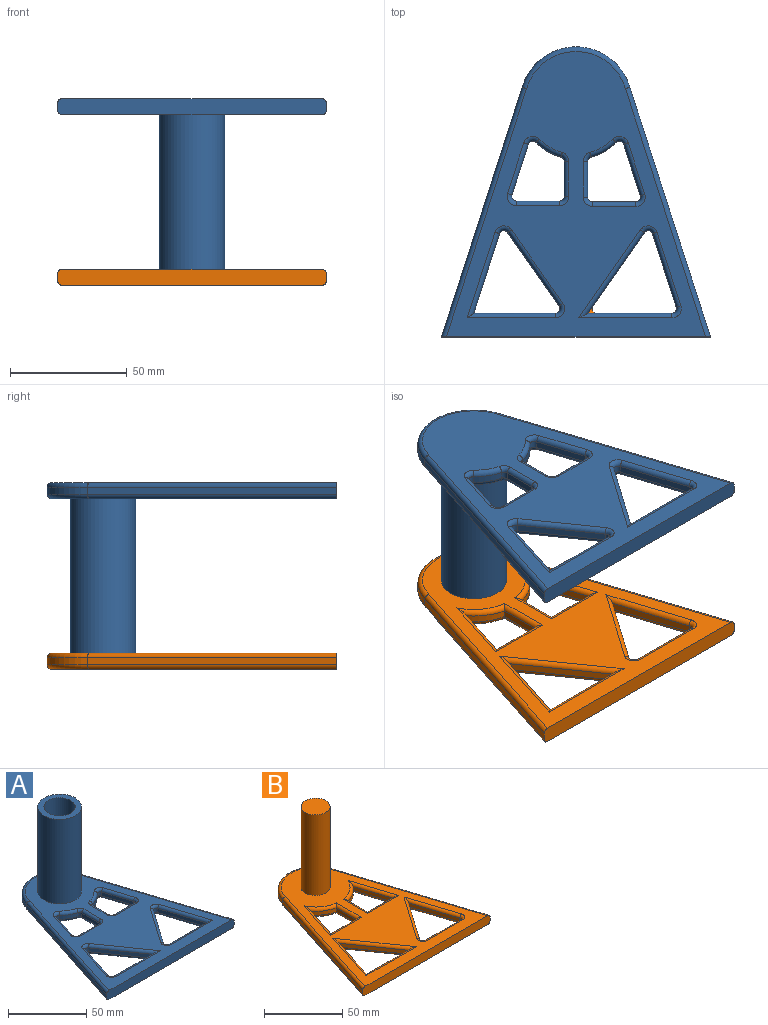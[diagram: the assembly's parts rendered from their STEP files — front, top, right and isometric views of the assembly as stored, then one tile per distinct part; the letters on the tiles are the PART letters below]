
ASSEMBLY  parts=2 mates=1
PART A: 100 faces, bbox 115x126.6x73 mm
  f0: cylinder r=24mm len=10.61mm, axis (0,0,-1), area 37.4mm2, adj f68,f73,f76,f79
  f1: plane 21.71x7.01mm, normal (-0.95,-0.31,0), area 68.4mm2, adj f66,f67,f75,f76
  f2: plane 18.51x3mm, normal (0,1,0), area 55.5mm2, adj f60,f64,f65,f66
  f3: plane 34.05x10.99mm, normal (-0.95,-0.31,0), area 107.3mm2, adj f4,f48,f53,f58
  f4: plane 34.92x3mm, normal (0,1,0), area 104.8mm2, adj f3,f50,f55,f59
  f5: plane 22.05x7.12mm, normal (0.95,-0.31,0), area 69.5mm2, adj f83,f84,f93,f94
  f6: cylinder r=24mm len=10.61mm, axis (0,0,-1), area 37.4mm2, adj f88,f93,f96,f99
  f7: plane 15.28x3mm, normal (-1,0,0), area 45.8mm2, adj f86,f87,f95,f96
  f8: plane 115x7mm, normal (0,-1,0), area 801.4mm2, adj f9,f15,f18,f19,f36,f38,f41,f47
  f9: plane 106.63x34.43mm, normal (0.95,0.31,0), area 336.1mm2, adj f8,f36,f40,f41
  f10: cylinder r=24mm len=46.1mm, axis (0,0,-1), area 185.6mm2, adj f39,f40,f44,f45
  f11: plane 36.01x3mm, normal (0,1,0), area 108mm2, adj f16,f27,f32,f35
  f12: plane 31.43x10.15mm, normal (0.95,-0.31,0), area 99.1mm2, adj f26,f28,f31,f32
  f13: plane 31.43x22.02mm, normal (0.82,-0.57,0), area 115.1mm2, adj f49,f53,f54,f55
  f14: plane 18.62x3mm, normal (0,1,0), area 55.9mm2, adj f80,f84,f85,f86
  f15: plane 106.63x34.43mm, normal (-0.95,0.31,0), area 336.1mm2, adj f8,f38,f44,f47
  f16: plane 34.58x24.23mm, normal (-0.82,-0.57,0), area 126.7mm2, adj f11,f24,f28,f33
  f17: plane 14.94x3mm, normal (1,0,0), area 44.8mm2, adj f63,f64,f73,f74
  f18: plane 122x110.8mm, normal (0,0,1), area 4813.2mm2, adj f8,f20,f30,f31,f33,f34,f35,f41
  f19: plane 122x110.8mm, normal (0,0,-1), area 5429mm2, adj f8,f24,f25,f26,f27,f29,f36,f37
  f20: cylinder r=14mm len=66mm, axis (0,0,-1), area 5805.7mm2, adj f18,f22
  f21: cylinder r=10mm len=66mm, axis (0,0,-1), area 4146.9mm2, adj f22,f23
  f22: plane 28x28mm, normal (0,0,1), area 301.6mm2, adj f20,f21
  f23: plane 20x20mm, normal (0,0,1), area 314.2mm2, adj f21
  f24: cylinder r=2mm len=38.87mm, axis (0.57,-0.82,0), area 137mm2, adj f16,f19,f25,f27
  f25: torus R=4mm, axis (0,0,1), area 19mm2, adj f19,f24,f26,f28
  f26: cylinder r=2mm len=32.05mm, axis (0.31,0.95,0), area 103.8mm2, adj f12,f19,f25,f29
  f27: cylinder r=2mm len=39.86mm, axis (-1,0,0), area 117.5mm2, adj f11,f19,f24,f29
  f28: cylinder r=2mm len=3.54mm, axis (0,0,-1), area 13.3mm2, adj f12,f16,f25,f30
  f29: torus R=4mm, axis (0,0,1), area 16.1mm2, adj f19,f26,f27,f32
  f30: torus R=4mm, axis (0,0,1), area 19mm2, adj f18,f28,f31,f33
  f31: cylinder r=2mm len=32.05mm, axis (-0.31,-0.95,0), area 103.8mm2, adj f12,f18,f30,f34
  f32: cylinder r=2mm len=3mm, axis (0,0,1), area 11.3mm2, adj f11,f12,f29,f34
  f33: cylinder r=2mm len=38.87mm, axis (-0.57,0.82,0), area 137mm2, adj f16,f18,f30,f35
  f34: torus R=4mm, axis (0,0,1), area 16.1mm2, adj f18,f31,f32,f35
  f35: cylinder r=2mm len=39.86mm, axis (1,0,0), area 117.5mm2, adj f11,f18,f33,f34
  f36: cylinder r=2mm len=107.24mm, axis (-0.31,0.95,0), area 351.3mm2, adj f8,f9,f19,f37
  f37: torus R=4mm, axis (0,0,1), area 0.3mm2, adj f19,f36,f39,f40
  f38: cylinder r=2mm len=107.24mm, axis (-0.31,-0.95,0), area 351.3mm2, adj f8,f15,f19,f42
  f39: torus R=22mm, axis (0,0,1), area 188.4mm2, adj f10,f19,f37,f42
  f40: cylinder r=2mm len=3mm, axis (0,0,-1), area 0.2mm2, adj f9,f10,f37,f43
  f41: cylinder r=2mm len=107.24mm, axis (0.31,-0.95,0), area 351.3mm2, adj f8,f9,f18,f43
  f42: torus R=4mm, axis (0,0,1), area 0.3mm2, adj f19,f38,f39,f44
  f43: torus R=4mm, axis (0,0,1), area 0.3mm2, adj f18,f40,f41,f45
  f44: cylinder r=2mm len=3mm, axis (0,0,-1), area 0.2mm2, adj f10,f15,f42,f46
  f45: torus R=22mm, axis (0,0,1), area 188.4mm2, adj f10,f18,f43,f46
  f46: torus R=4mm, axis (0,0,1), area 0.3mm2, adj f18,f44,f45,f47
  f47: cylinder r=2mm len=107.24mm, axis (0.31,0.95,0), area 351.3mm2, adj f8,f15,f18,f46
  f48: cylinder r=2mm len=37.27mm, axis (0.31,-0.95,0), area 115.5mm2, adj f3,f19,f50,f51
  f49: cylinder r=2mm len=32.58mm, axis (0.57,0.82,0), area 120.6mm2, adj f13,f19,f51,f52
  f50: cylinder r=2mm len=37.67mm, axis (-1,0,0), area 112.8mm2, adj f4,f19,f48,f52
  f51: torus R=4mm, axis (0,0,1), area 19mm2, adj f19,f48,f49,f53
  f52: torus R=4mm, axis (0,0,1), area 18.7mm2, adj f19,f49,f50,f55
  f53: cylinder r=2mm len=3.54mm, axis (0,0,-1), area 13.3mm2, adj f3,f13,f51,f56
  f54: cylinder r=2mm len=32.58mm, axis (-0.57,-0.82,0), area 120.6mm2, adj f13,f18,f56,f57
  f55: cylinder r=2mm len=3.15mm, axis (0,0,-1), area 13.1mm2, adj f4,f13,f52,f57
  f56: torus R=4mm, axis (0,0,1), area 19mm2, adj f18,f53,f54,f58
  f57: torus R=4mm, axis (0,0,1), area 18.7mm2, adj f18,f54,f55,f59
  f58: cylinder r=2mm len=37.27mm, axis (-0.31,0.95,0), area 115.5mm2, adj f3,f18,f56,f59
  f59: cylinder r=2mm len=37.67mm, axis (1,0,0), area 112.8mm2, adj f4,f18,f57,f58
  f60: cylinder r=2mm len=18.51mm, axis (-1,0,0), area 58.1mm2, adj f2,f19,f61,f62
  f61: torus R=4mm, axis (0,0,1), area 13.5mm2, adj f19,f60,f63,f64
  f62: torus R=4mm, axis (0,0,1), area 16.1mm2, adj f19,f60,f66,f67
  f63: cylinder r=2mm len=14.94mm, axis (0,1,0), area 46.9mm2, adj f17,f19,f61,f69
  f64: cylinder r=2mm len=3mm, axis (0,0,-1), area 9.4mm2, adj f2,f17,f61,f70
  f65: cylinder r=2mm len=18.51mm, axis (1,0,0), area 58.1mm2, adj f2,f18,f70,f71
  f66: cylinder r=2mm len=3mm, axis (0,0,1), area 11.3mm2, adj f1,f2,f62,f71
  f67: cylinder r=2mm len=22.32mm, axis (0.31,-0.95,0), area 71.7mm2, adj f1,f19,f62,f72
  f68: torus R=22mm, axis (0,0,1), area 37.9mm2, adj f0,f19,f69,f72
  f69: torus R=4mm, axis (0,0,1), area 11.1mm2, adj f19,f63,f68,f73
  f70: torus R=4mm, axis (0,0,1), area 13.5mm2, adj f18,f64,f65,f74
  f71: torus R=4mm, axis (0,0,1), area 16.1mm2, adj f18,f65,f66,f75
  f72: torus R=4mm, axis (0,0,1), area 17.6mm2, adj f19,f67,f68,f76
  f73: cylinder r=2mm len=3mm, axis (0,0,-1), area 7.8mm2, adj f0,f17,f69,f77
  f74: cylinder r=2mm len=14.94mm, axis (0,-1,0), area 46.9mm2, adj f17,f18,f70,f77
  f75: cylinder r=2mm len=22.32mm, axis (-0.31,0.95,0), area 71.7mm2, adj f1,f18,f71,f78
  f76: cylinder r=2mm len=3.33mm, axis (0,0,-1), area 12.3mm2, adj f0,f1,f72,f78
  f77: torus R=4mm, axis (0,0,1), area 11.1mm2, adj f18,f73,f74,f79
  f78: torus R=4mm, axis (0,0,1), area 17.6mm2, adj f18,f75,f76,f79
  f79: torus R=22mm, axis (0,0,1), area 37.9mm2, adj f0,f18,f77,f78
  f80: cylinder r=2mm len=18.62mm, axis (-1,0,0), area 58.5mm2, adj f14,f19,f81,f82
  f81: torus R=4mm, axis (0,0,1), area 16.1mm2, adj f19,f80,f83,f84
  f82: torus R=4mm, axis (0,0,1), area 13.5mm2, adj f19,f80,f86,f87
  f83: cylinder r=2mm len=22.67mm, axis (0.31,0.95,0), area 72.8mm2, adj f5,f19,f81,f89
  f84: cylinder r=2mm len=3mm, axis (0,0,1), area 11.3mm2, adj f5,f14,f81,f90
  f85: cylinder r=2mm len=18.62mm, axis (1,0,0), area 58.5mm2, adj f14,f18,f90,f91
  f86: cylinder r=2mm len=3mm, axis (0,0,-1), area 9.4mm2, adj f7,f14,f82,f91
  f87: cylinder r=2mm len=15.28mm, axis (0,-1,0), area 48mm2, adj f7,f19,f82,f92
  f88: torus R=22mm, axis (0,0,1), area 37.9mm2, adj f6,f19,f89,f92
  f89: torus R=4mm, axis (0,0,1), area 17.6mm2, adj f19,f83,f88,f93
  f90: torus R=4mm, axis (0,0,1), area 16.1mm2, adj f18,f84,f85,f94
  f91: torus R=4mm, axis (0,0,1), area 13.5mm2, adj f18,f85,f86,f95
  f92: torus R=4mm, axis (0,0,1), area 11.1mm2, adj f19,f87,f88,f96
  f93: cylinder r=2mm len=3.33mm, axis (0,0,-1), area 12.3mm2, adj f5,f6,f89,f97
  f94: cylinder r=2mm len=22.67mm, axis (-0.31,-0.95,0), area 72.8mm2, adj f5,f18,f90,f97
  f95: cylinder r=2mm len=15.28mm, axis (0,1,0), area 48mm2, adj f7,f18,f91,f98
  f96: cylinder r=2mm len=3mm, axis (0,0,-1), area 7.8mm2, adj f6,f7,f92,f98
  f97: torus R=4mm, axis (0,0,1), area 17.6mm2, adj f18,f93,f94,f99
  f98: torus R=4mm, axis (0,0,1), area 11.1mm2, adj f18,f95,f96,f99
  f99: torus R=22mm, axis (0,0,1), area 37.9mm2, adj f6,f18,f97,f98
PART B: 62 faces, bbox 115x126.6x70 mm
  f0: cylinder r=9.25mm len=63mm, axis (0,0,-1), area 3661.5mm2, adj f1,f20
  f1: plane 18.5x18.5mm, normal (0,0,1), area 268.8mm2, adj f0
  f2: plane 38.76x3mm, normal (0,1,0), area 116.3mm2, adj f3,f19,f37,f48
  f3: plane 37.87x12.23mm, normal (0.95,-0.31,0), area 119.4mm2, adj f2,f19,f39,f50
  f4: plane 34.72x24.33mm, normal (0.82,-0.57,0), area 127.2mm2, adj f5,f25,f26,f29
  f5: plane 35.26x11.38mm, normal (-0.95,-0.31,0), area 111.1mm2, adj f4,f30,f33,f36
  f6: cylinder r=24mm len=14.3mm, axis (0,0,-1), area 52.2mm2, adj f7,f16,f40,f57
  f7: plane 18.85x3mm, normal (-1,0,0), area 56.5mm2, adj f6,f8,f41,f56
  f8: plane 23.37x3mm, normal (0,1,0), area 70.1mm2, adj f7,f16,f43,f54
  f9: plane 106.66x34.44mm, normal (0.95,0.31,0), area 336.2mm2, adj f10,f17,f22,f51
  f10: cylinder r=24mm len=46.12mm, axis (0,0,-1), area 185.7mm2, adj f9,f11,f23,f53
  f11: plane 106.66x34.44mm, normal (-0.95,0.31,0), area 336.2mm2, adj f10,f17,f24,f52
  f12: plane 18.51x3mm, normal (1,0,0), area 55.5mm2, adj f13,f18,f44,f58
  f13: cylinder r=24mm len=14.3mm, axis (0,0,-1), area 52.2mm2, adj f12,f14,f46,f60
  f14: plane 27.72x8.95mm, normal (-0.95,-0.31,0), area 87.4mm2, adj f13,f18,f47,f61
  f15: plane 32.17x3mm, normal (0,1,0), area 96.5mm2, adj f25,f31,f32,f36
  f16: plane 28.06x9.06mm, normal (0.95,-0.31,0), area 88.5mm2, adj f6,f8,f42,f55
  f17: plane 115x7mm, normal (0,-1,0), area 801.4mm2, adj f9,f11,f20,f21,f22,f24,f51,f52
  f18: plane 23.26x3mm, normal (0,1,0), area 69.8mm2, adj f12,f14,f45,f59
  f19: plane 37.87x26.53mm, normal (-0.82,-0.57,0), area 138.7mm2, adj f2,f3,f38,f49
  f20: plane 122x110.8mm, normal (0,0,1), area 5081.8mm2, adj f0,f17,f26,f27,f30,f31,f34,f48
  f21: plane 122x110.8mm, normal (0,0,-1), area 5350.6mm2, adj f17,f22,f23,f24,f28,f29,f32,f33
  f22: cylinder r=2mm len=107.3mm, axis (-0.31,0.95,0), area 351.4mm2, adj f9,f17,f21,f23
  f23: torus R=22mm, axis (0,0,1), area 188.7mm2, adj f10,f21,f22,f24
  f24: cylinder r=2mm len=107.3mm, axis (-0.31,-0.95,0), area 351.4mm2, adj f11,f17,f21,f23
  f25: cylinder r=2mm len=3.15mm, axis (0,0,-1), area 13.1mm2, adj f4,f15,f27,f28
  f26: cylinder r=2mm len=39.16mm, axis (-0.57,-0.82,0), area 137.8mm2, adj f4,f20,f27,f30
  f27: torus R=4mm, axis (0,0,1), area 18.7mm2, adj f20,f25,f26,f31
  f28: torus R=4mm, axis (0,0,1), area 18.7mm2, adj f21,f25,f29,f32
  f29: cylinder r=2mm len=39.16mm, axis (0.57,0.82,0), area 137.8mm2, adj f4,f21,f28,f33
  f30: cylinder r=2mm len=39.69mm, axis (-0.31,0.95,0), area 121mm2, adj f5,f20,f26,f34
  f31: cylinder r=2mm len=32.17mm, axis (1,0,0), area 101.1mm2, adj f15,f20,f27,f34
  f32: cylinder r=2mm len=32.17mm, axis (-1,0,0), area 101.1mm2, adj f15,f21,f28,f35
  f33: cylinder r=2mm len=39.69mm, axis (0.31,-0.95,0), area 121mm2, adj f5,f21,f29,f35
  f34: torus R=4mm, axis (0,0,1), area 16.1mm2, adj f20,f30,f31,f36
  f35: torus R=4mm, axis (0,0,1), area 16.1mm2, adj f21,f32,f33,f36
  f36: cylinder r=2mm len=3mm, axis (0,0,1), area 11.3mm2, adj f5,f15,f34,f35
  f37: cylinder r=2mm len=45.35mm, axis (-1,0,0), area 129.3mm2, adj f2,f21,f38,f39
  f38: cylinder r=2mm len=45.46mm, axis (0.57,-0.82,0), area 154.2mm2, adj f19,f21,f37,f39
  f39: cylinder r=2mm len=44.92mm, axis (0.31,0.95,0), area 132.7mm2, adj f3,f21,f37,f38
  f40: torus R=22mm, axis (0,0,1), area 59.5mm2, adj f6,f21,f41,f42
  f41: cylinder r=2mm len=22.53mm, axis (0,-1,0), area 63.4mm2, adj f7,f21,f40,f43
  f42: cylinder r=2mm len=35.47mm, axis (0.31,0.95,0), area 100.6mm2, adj f16,f21,f40,f43
  f43: cylinder r=2mm len=28.11mm, axis (-1,0,0), area 78.8mm2, adj f8,f21,f41,f42
  f44: cylinder r=2mm len=22.18mm, axis (0,1,0), area 62.3mm2, adj f12,f21,f45,f46
  f45: cylinder r=2mm len=28mm, axis (-1,0,0), area 78.5mm2, adj f18,f21,f44,f47
  f46: torus R=22mm, axis (0,0,1), area 59.5mm2, adj f13,f21,f44,f47
  f47: cylinder r=2mm len=35.13mm, axis (0.31,-0.95,0), area 99.4mm2, adj f14,f21,f45,f46
  f48: cylinder r=2mm len=45.35mm, axis (1,0,0), area 129.3mm2, adj f2,f20,f49,f50
  f49: cylinder r=2mm len=45.46mm, axis (-0.57,0.82,0), area 154.2mm2, adj f19,f20,f48,f50
  f50: cylinder r=2mm len=44.92mm, axis (-0.31,-0.95,0), area 132.7mm2, adj f3,f20,f48,f49
  f51: cylinder r=2mm len=107.3mm, axis (0.31,-0.95,0), area 351.4mm2, adj f9,f17,f20,f53
  f52: cylinder r=2mm len=107.3mm, axis (0.31,0.95,0), area 351.4mm2, adj f11,f17,f20,f53
  f53: torus R=22mm, axis (0,0,1), area 188.7mm2, adj f10,f20,f51,f52
  f54: cylinder r=2mm len=28.11mm, axis (1,0,0), area 78.8mm2, adj f8,f20,f55,f56
  f55: cylinder r=2mm len=35.47mm, axis (-0.31,-0.95,0), area 100.6mm2, adj f16,f20,f54,f57
  f56: cylinder r=2mm len=22.53mm, axis (0,1,0), area 63.4mm2, adj f7,f20,f54,f57
  f57: torus R=22mm, axis (0,0,1), area 59.5mm2, adj f6,f20,f55,f56
  f58: cylinder r=2mm len=22.18mm, axis (0,-1,0), area 62.3mm2, adj f12,f20,f59,f60
  f59: cylinder r=2mm len=28mm, axis (1,0,0), area 78.5mm2, adj f18,f20,f58,f61
  f60: torus R=22mm, axis (0,0,1), area 59.5mm2, adj f13,f20,f58,f61
  f61: cylinder r=2mm len=35.13mm, axis (-0.31,0.95,0), area 99.4mm2, adj f14,f20,f59,f60
PLACE A rot(axis=(0,-1,0),180deg) t=(0.37,57.24,90.65)mm
PLACE B t=(-3.1,-3.42,10.65)mm
MATE cylindrical A.f0 <-> B.f0  axis (0,0,1) through (0.37,57.24,17.65)mm
